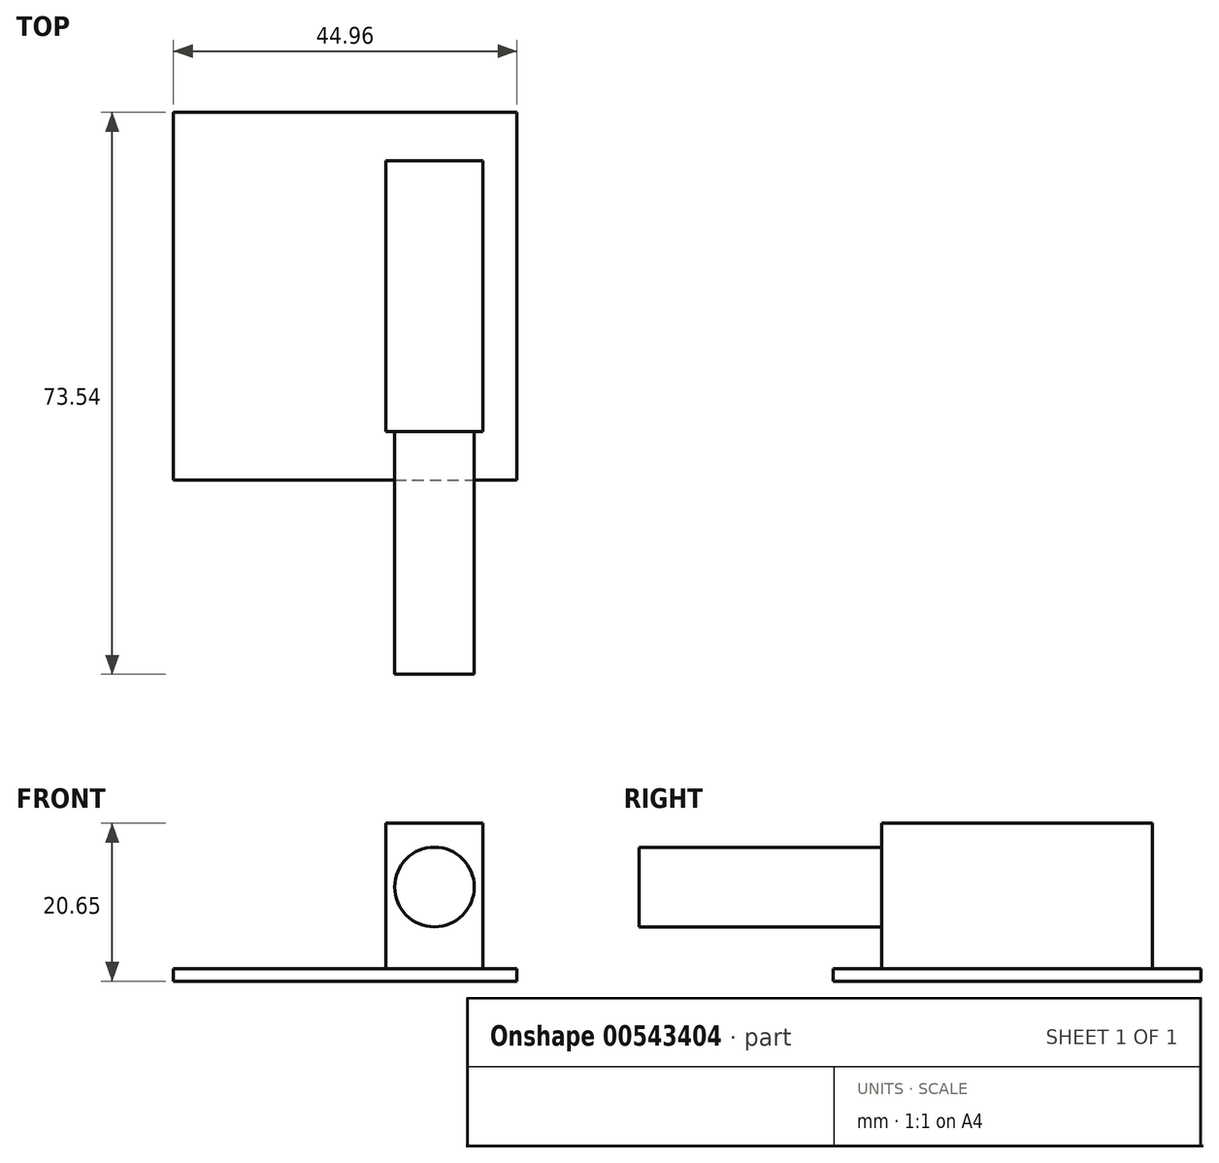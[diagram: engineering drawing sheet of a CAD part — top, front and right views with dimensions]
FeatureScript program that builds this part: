
annotation { "Feature Type Name" : "Feature", "Feature Type Description" : "" }
export const myFeature = defineFeature(function(context is Context, id is Id, definition is map)
    precondition{}
    {
        {
            var Q0;
            Q0=qCreatedBy(makeId("Top.planeOp"),FACE);
            var sketch = newSketch(context, id + "F0", { "sketchPlane" : qUnion([Q0])});
            skLineSegment(sketch, "E0.bottom", {"start": v(-22.48, 24.07) * mm, "end": v(22.48, 24.07) * mm});
            skLineSegment(sketch, "E0.top", {"start": v(-22.48, -24.07) * mm, "end": v(22.48, -24.07) * mm});
            skLineSegment(sketch, "E0.left", {"start": v(-22.48, 24.07) * mm, "end": v(-22.48, -24.07) * mm});
            skLineSegment(sketch, "E0.right", {"start": v(22.48, 24.07) * mm, "end": v(22.48, -24.07) * mm});
            skPoint(sketch, "E0.middle", {"position": v(0, 0) * mm});
            skSolve(sketch);
        }
        {
            var Q0;
            Q0 = qSketchRegion(id + "F0", true);
            extrude(context, id + "F1", {"entities" : qUnion([Q0]), "endBound" : BoundingType.SYMMETRIC, "depth" : 1.6 * mm, "offsetDistance" : 25.4 * mm});
        }
        {
            var Q0;
            Q0=makeQuery(id+"F1.opExtrude","SWEPT_FACE",FACE,{"disambiguationData":[OSD([sQuery(id+"F0.wireOp",EDGE,"E0.top")])]});
            var sketch = newSketch(context, id + "F2", { "sketchPlane" : qUnion([Q0])});
            skCircle(sketch, "E1", {"center": v(11.68, 11.52) * mm, "radius": 5.2 * mm});
            skPoint(sketch, "E2", {"position": v(6.48, 11.52) * mm});
            skPoint(sketch, "E3", {"position": v(11.68, 16.73) * mm});
            skSolve(sketch);
        }
        {
            var Q0;
            Q0 = qSketchRegion(id + "F2", true);
            extrude(context, id + "F3", {"entities" : qUnion([Q0]), "depth" : 25.4 * mm, "offsetDistance" : 25.4 * mm, "hasSecondDirection" : true, "secondDirectionOppositeDirection" : true, "secondDirectionDepth" : 6.35 * mm});
        }
        {
            var Q0;
            Q0=makeQuery(id+"F1.opExtrude","CAP_FACE",FACE,{"disambiguationData":[OSD([sQuery(id+"F0.wireOp",EDGE,"E0.bottom"),sQuery(id+"F0.wireOp",EDGE,"E0.top"),sQuery(id+"F0.wireOp",EDGE,"E0.left"),sQuery(id+"F0.wireOp",EDGE,"E0.right")])],"isStart":false});
            var sketch = newSketch(context, id + "F4", { "sketchPlane" : qUnion([Q0])});
            skLineSegment(sketch, "E4.bottom", {"start": v(18.03, 17.72) * mm, "end": v(5.33, 17.72) * mm});
            skLineSegment(sketch, "E4.top", {"start": v(18.03, -17.72) * mm, "end": v(5.33, -17.72) * mm});
            skLineSegment(sketch, "E4.left", {"start": v(18.03, 17.72) * mm, "end": v(18.03, -17.72) * mm});
            skLineSegment(sketch, "E4.right", {"start": v(5.33, 17.72) * mm, "end": v(5.33, -17.72) * mm});
            skPoint(sketch, "E4.middle", {"position": v(11.68, 0) * mm});
            skLineSegment(sketch, "E5.0", {"start": v(16.9, -17.72) * mm, "end": v(6.48, -17.72) * mm, "construction": true});
            skPoint(sketch, "E6", {"position": v(11.68, -17.72) * mm});
            skSolve(sketch);
        }
        {
            var Q0;
            Q0=makeQuery(id+"F4.imprint","IMPRINT",FACE,{"disambiguationData":[TD([[makeQuery(id+"F4.imprint","IMPRINT",EDGE,{"derivedFrom":sQuery(id+"F4.wireOp",EDGE,"E4.bottom")}),1.0]])]});
            extrude(context, id + "F5", {"entities" : qUnion([Q0]), "depth" : 19.05 * mm, "offsetDistance" : 25.4 * mm});
        }
    });
